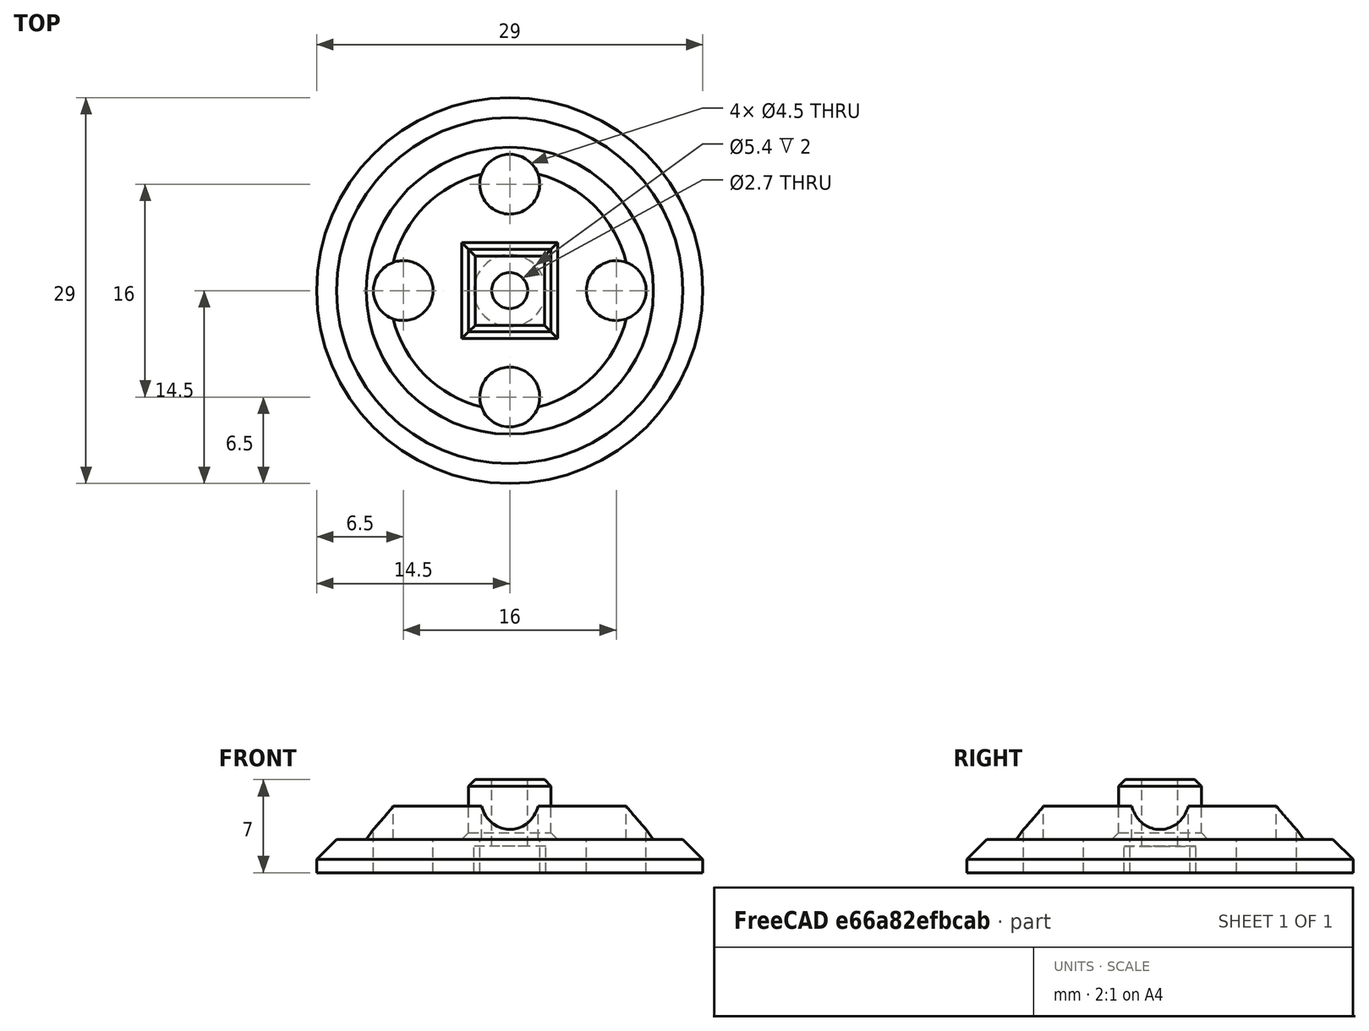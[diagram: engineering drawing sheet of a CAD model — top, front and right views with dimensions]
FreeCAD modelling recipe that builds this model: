
FCSTD DOCUMENT  (FreeCAD 0.15R4671 (Git))
Label: tendon_wheel_ax_9_15_mm_top
License: CC-BY 3.0
LicenseURL: http://creativecommons.org/licenses/by/3.0/
objects: Part::Cylinder×8, Part::MultiFuse×4, Part::Cut×3, Part::Chamfer×3, Part::Cone×1, Part::Box×1
note: 20 computed .brp shape members not serialized (recipe doc carries the construction recipe); baked Part::Feature solids carry a one-line shape summary decoded from their .brp

FEATURE [Part::Cylinder] Cylinder
  Angle = 360
  Height = 6
  Placement = pos=(0,0,2) rot=(0,0,1;0rad)
  Radius = 9
FEATURE [Part::Cylinder] Cylinder001
  Angle = 360
  Height = 2.5
  Placement = pos=(0,0,-0.5) rot=(0,0,1;0rad)
  Radius = 14.5
FEATURE [Part::Cone] Cone
  Angle = 360
  Height = 3.5
  Placement = pos=(0,0,1) rot=(0,0,1;0rad)
  Radius1 = 11.5
  Radius2 = 9
FEATURE [Part::Box] Box  label="Cube"
  Height = 4.5
  Length = 6.2
  Placement = pos=(-3.1,-3.1,2) rot=(0,0,1;0rad)
  Width = 6.2
FEATURE [Part::MultiFuse] Fusion
  Shapes = -> [Cone,Cylinder001]
FEATURE [Part::Cylinder] Cylinder002  label="Cylinder004"
  Angle = 360
  Height = 20
  Placement = pos=(0,0,-5) rot=(0,0,1;0rad)
  Radius = 1.35
FEATURE [Part::Cut] Cut
  Base = -> Fusion
  Tool = -> Cylinder
FEATURE [Part::MultiFuse] Fusion001
  Shapes = -> [Cut,Box]
FEATURE [Part::Cylinder] Cylinder003  label="Cylinder012"
  Angle = 360
  Height = 2
  Placement = pos=(0,0,-0.5) rot=(0,0,1;0rad)
  Radius = 2.7
FEATURE [Part::MultiFuse] Fusion002
  Shapes = -> [Cylinder003,Cylinder002]
FEATURE [Part::Cut] Cut001
  Base = -> Fusion001
  Tool = -> Fusion002
FEATURE [Part::Chamfer] Chamfer
  Base = -> Cut001
  Edges = 4 edges r=0.5: [Edge1,Edge2,Edge3,Edge4]
FEATURE [Part::Cylinder] Cylinder005  label="TopHole005"
  Angle = 360
  Height = 20
  Placement = pos=(8,0,-4) rot=(0,0,1;0rad)
  Radius = 2.25
FEATURE [Part::Cylinder] Cylinder008  label="TopHole006"
  Angle = 360
  Height = 20
  Placement = pos=(0,8,-4) rot=(0,0,1;0rad)
  Radius = 2.25
FEATURE [Part::Cylinder] Cylinder009  label="TopHole004"
  Angle = 360
  Height = 20
  Placement = pos=(-8,0,-4) rot=(0,0,1;0rad)
  Radius = 2.25
FEATURE [Part::Cylinder] Cylinder011  label="TopHole007"
  Angle = 360
  Height = 20
  Placement = pos=(0,-8,-4) rot=(0,0,1;0rad)
  Radius = 2.25
FEATURE [Part::MultiFuse] Fusion003
  Shapes = -> [Cylinder011,Cylinder008,Cylinder009,Cylinder005]
FEATURE [Part::Cut] Cut002
  Base = -> Chamfer
  Tool = -> Fusion003
FEATURE [Part::Chamfer] Chamfer001
  Base = -> Cut002
  Edges = 4 edges r=0.5: [Edge17,Edge20,Edge22,Edge23]
FEATURE [Part::Chamfer] Chamfer002
  Base = -> Chamfer001
  Edges = 1 edges r=1.5: [Edge73]
